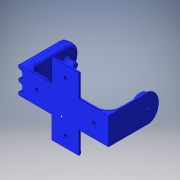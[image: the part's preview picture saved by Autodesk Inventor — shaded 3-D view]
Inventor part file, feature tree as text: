
AUTODESK INVENTOR PART (.ipt)
format: ipt  version: 2016 (Build 200138000, 138)  size: 588,288 bytes
history: native  units: in
note: dims shown in document units (in); Inventor stores cm internally (conversion verified against a paired STEP export)
features: sketch x12, other x3
ambient origin geometry x8: Origin, YZ Plane, XZ Plane, XY Plane, X Axis, Y Axis, Z Axis, Center Point
bodies: Solid1 (feature_tree)
feature tree (15):
  other  "Hip_side.ipt"
  other  "Solid1::Hip_side.ipt"
  other  "TaggingFeature1"
  sketch  "Sketch1"  dims[d0=0.3937in]
  sketch  "Sketch4"
  sketch  "Sketch5"
  sketch  "Sketch7"
  sketch  "Sketch9"
  sketch  "Sketch10"
  sketch  "Sketch15"
  sketch  "Sketch16"
  sketch  "Sketch17"
  sketch  "Sketch18"
  sketch  "Sketch19"
  sketch  "Sketch20"
